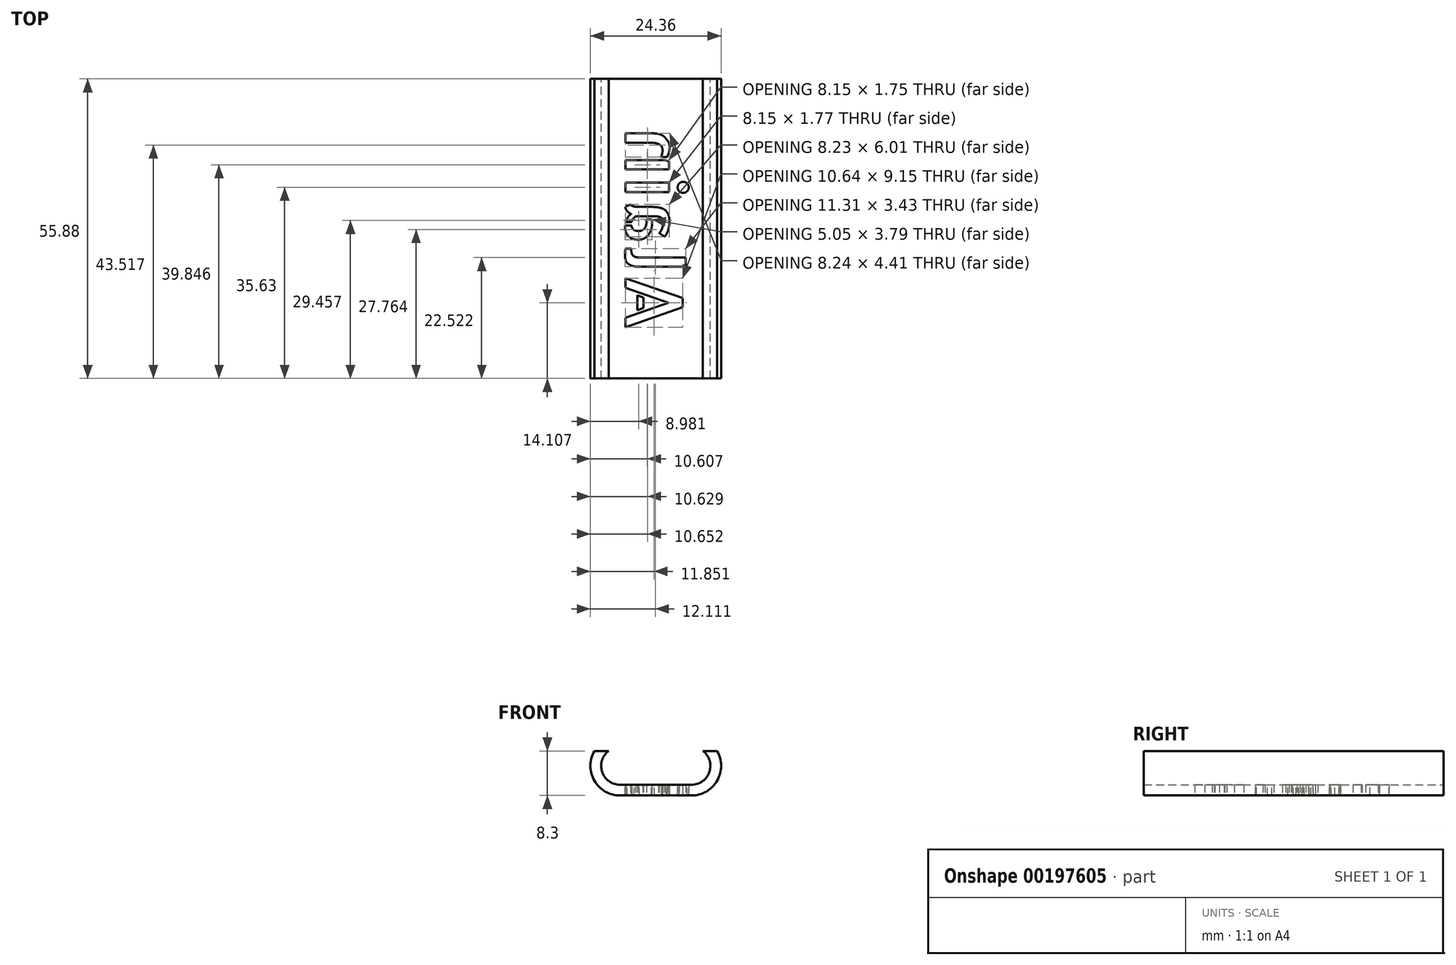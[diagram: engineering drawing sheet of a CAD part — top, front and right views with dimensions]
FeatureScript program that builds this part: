
annotation { "Feature Type Name" : "Feature", "Feature Type Description" : "" }
export const myFeature = defineFeature(function(context is Context, id is Id, definition is map)
    precondition{}
    {
        {
            var Q0;
            Q0=qCreatedBy(makeId("Front.planeOp"),FACE);
            var sketch = newSketch(context, id + "F0", { "sketchPlane" : qUnion([Q0])});
            skLineSegment(sketch, "E0.bottom", {"start": v(-6.67, 3.5) * mm, "end": v(6.67, 3.5) * mm});
            skLineSegment(sketch, "E1.bottom", {"start": v(-6.67, -3.5) * mm, "end": v(6.67, -3.5) * mm});
            skArc(sketch, "E2", {"start": v(-6.67, 3.5) * mm, "mid": v(-10.17, 0) * mm, "end": v(-6.67, -3.5) * mm});
            skArc(sketch, "E3", {"start": v(6.67, -3.5) * mm, "mid": v(10.17, 0) * mm, "end": v(6.67, 3.5) * mm});
            skArc(sketch, "E4.0", {"start": v(6.67, -5.51) * mm, "mid": v(12.18, 0) * mm, "end": v(6.67, 5.51) * mm});
            skLineSegment(sketch, "E5.0", {"start": v(-6.67, 5.51) * mm, "end": v(6.67, 5.51) * mm});
            skArc(sketch, "E6.0", {"start": v(-6.67, 5.51) * mm, "mid": v(-12.18, 0) * mm, "end": v(-6.67, -5.51) * mm});
            skLineSegment(sketch, "E7.0", {"start": v(-6.67, -5.51) * mm, "end": v(6.67, -5.51) * mm});
            skSolve(sketch);
        }
        {
            var Q0;
            Q0=makeQuery(id+"F0.imprint","IMPRINT",FACE,{"disambiguationData":[TD([[makeQuery(id+"F0.imprint","IMPRINT",EDGE,{"derivedFrom":sQuery(id+"F0.wireOp",EDGE,"E0.bottom")}),1.0]])]});
            extrude(context, id + "F1", {"entities" : qUnion([Q0]), "depth" : 55.88 * mm});
        }
        {
            var Q0;
            Q0=qCreatedBy(makeId("Front.planeOp"),FACE);
            var sketch = newSketch(context, id + "F2", { "sketchPlane" : qUnion([Q0])});
            skLineSegment(sketch, "E8.bottom", {"start": v(-13.47, 9.45) * mm, "end": v(13.57, 9.45) * mm});
            skLineSegment(sketch, "E8.top", {"start": v(-13.47, 2.8) * mm, "end": v(13.57, 2.8) * mm});
            skLineSegment(sketch, "E8.left", {"start": v(-13.47, 9.45) * mm, "end": v(-13.47, 2.8) * mm});
            skLineSegment(sketch, "E8.right", {"start": v(13.57, 9.45) * mm, "end": v(13.57, 2.8) * mm});
            skSolve(sketch);
        }
        {
            var Q0;
            Q0=makeQuery(id+"F2.imprint","IMPRINT",FACE,{"disambiguationData":[TD([[makeQuery(id+"F2.imprint","IMPRINT",EDGE,{"derivedFrom":sQuery(id+"F2.wireOp",EDGE,"E8.bottom")}),-1.0]])]});
            extrude(context, id + "F3", {"entities" : qUnion([Q0]), "operationType" : NewBodyOperationType.REMOVE, "depth" : 64.77 * mm});
        }
        {
            var Q0;
            Q0=makeQuery(id+"F1.opExtrude","SWEPT_FACE",FACE,{"disambiguationData":[OSD([sQuery(id+"F0.wireOp",EDGE,"E7.0")])]});
            var sketch = newSketch(context, id + "F4", { "sketchPlane" : qUnion([Q0])});
            skText(sketch, "E9", { "text": "Alain", "fontName": "AllertaStencil-Regular.ttf"});
            const initialGuessF4  = {"E9": [-0.00565, 0.04726, 0, -1, 0.01066]};
            skSetInitialGuess(sketch, initialGuessF4);
            skSolve(sketch);
        }
        {
            var Q0;
            Q0 = qSketchRegion(id + "F4", true);
            extrude(context, id + "F5", {"entities" : qUnion([Q0]), "operationType" : NewBodyOperationType.REMOVE, "oppositeDirection" : true, "depth" : 6.35 * mm});
        }
    });
